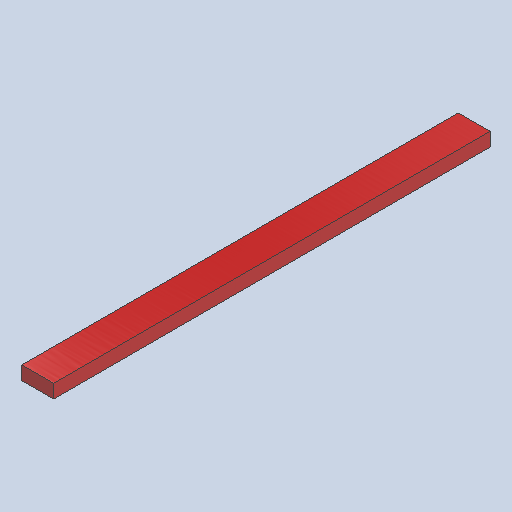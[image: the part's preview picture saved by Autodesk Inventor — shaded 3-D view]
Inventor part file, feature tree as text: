
AUTODESK INVENTOR PART (.ipt)
format: ipt  version: 2025 (Build 290162000, 162)  size: 96,256 bytes
history: native  units: in
note: dims shown in document units (in); Inventor stores cm internally (conversion verified against a paired STEP export)
features: other x4, sketch x1
ambient origin geometry x8: Origin, YZ Plane, XZ Plane, XY Plane, X Axis, Y Axis, Z Axis, Center Point
bodies: Solid1 (feature_tree)
feature tree (5):
  other  "4x2x4_MIR.ipt"
  other  "Solid1::4x2x4_MIR.ipt"
  other  "TaggingFeature1"
  sketch  "Sketch1"  dims[d0=0.3937in]
  other  "Finish1"
